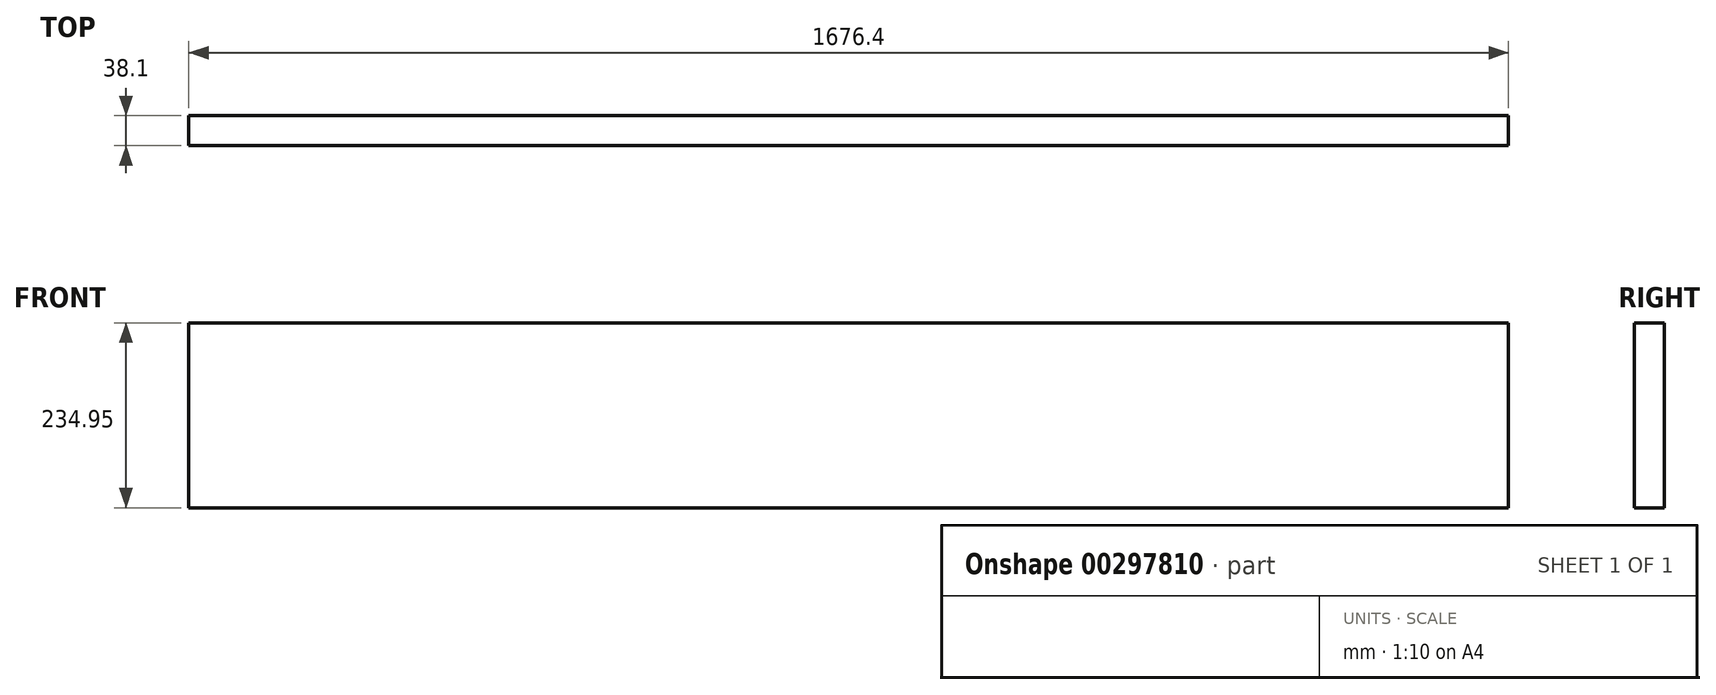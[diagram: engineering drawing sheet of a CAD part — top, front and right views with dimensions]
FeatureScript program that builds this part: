
annotation { "Feature Type Name" : "Feature", "Feature Type Description" : "" }
export const myFeature = defineFeature(function(context is Context, id is Id, definition is map)
    precondition{}
    {
        {
            var Q0;
            Q0=qCreatedBy(makeId("Front.planeOp"),FACE);
            var sketch = newSketch(context, id + "F0", { "sketchPlane" : qUnion([Q0])});
            skLineSegment(sketch, "E0.bottom", {"start": v(0, 0) * mm, "end": v(1676.4, 0) * mm});
            skLineSegment(sketch, "E0.top", {"start": v(0, 234.95) * mm, "end": v(1676.4, 234.95) * mm});
            skLineSegment(sketch, "E0.left", {"start": v(0, 0) * mm, "end": v(0, 234.95) * mm});
            skLineSegment(sketch, "E0.right", {"start": v(1676.4, 0) * mm, "end": v(1676.4, 234.95) * mm});
            skSolve(sketch);
        }
        {
            var Q0;
            Q0=makeQuery(id+"F0.imprint","IMPRINT",FACE,{"disambiguationData":[TD([[makeQuery(id+"F0.imprint","IMPRINT",EDGE,{"derivedFrom":sQuery(id+"F0.wireOp",EDGE,"E0.bottom")}),1.0]])]});
            extrude(context, id + "F1", {"entities" : qUnion([Q0]), "depth" : 38.1 * mm});
        }
    });
